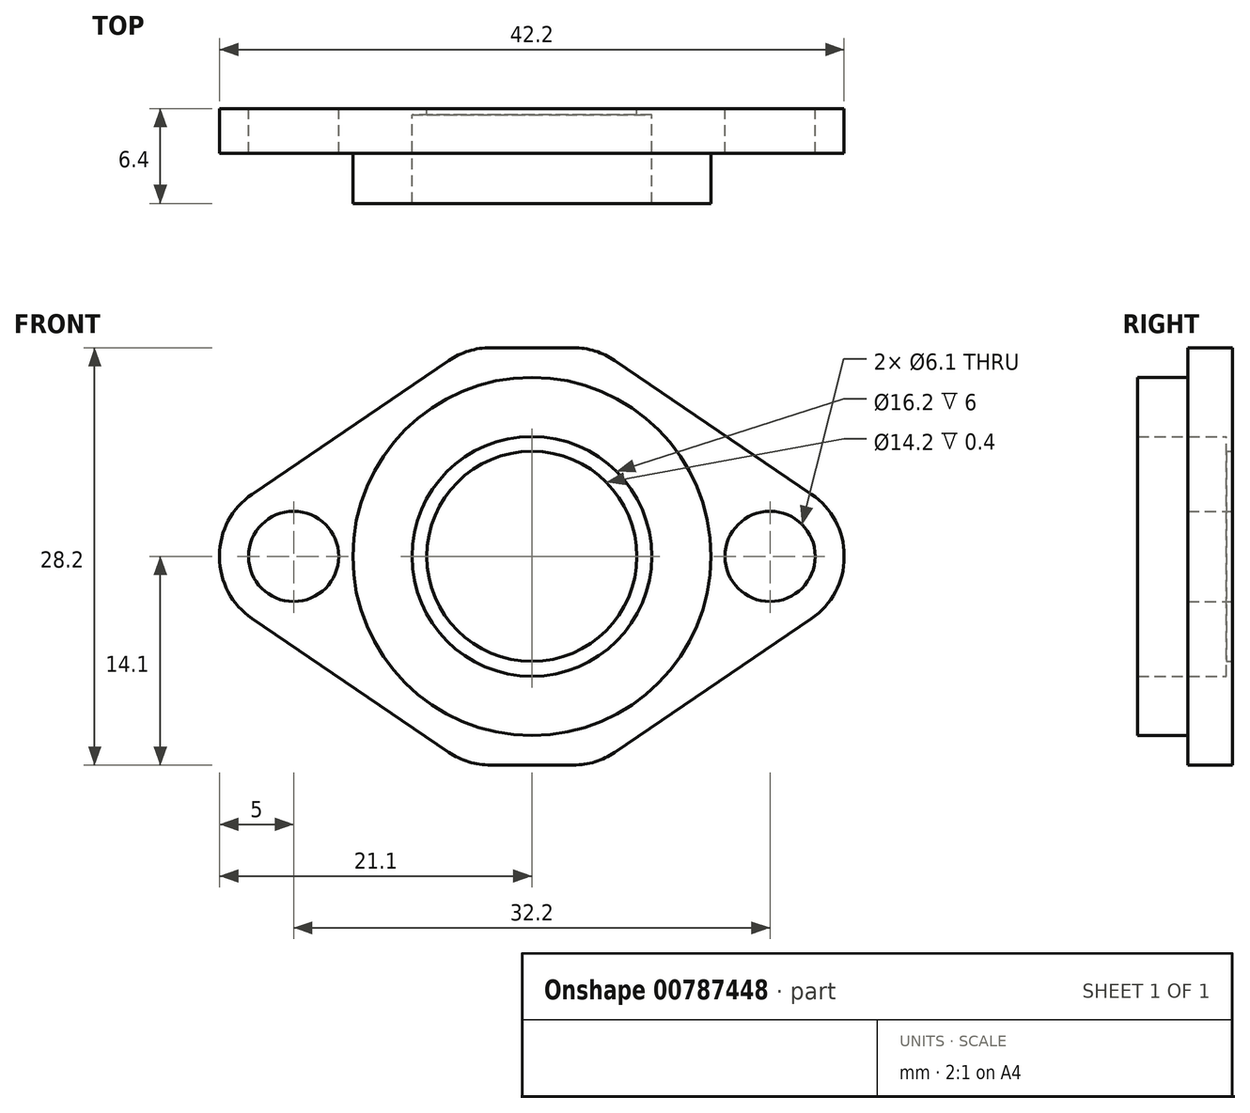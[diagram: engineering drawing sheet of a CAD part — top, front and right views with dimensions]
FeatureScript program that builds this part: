
annotation { "Feature Type Name" : "Feature", "Feature Type Description" : "" }
export const myFeature = defineFeature(function(context is Context, id is Id, definition is map)
    precondition{}
    {
        {
            var Q0;
            Q0=qCreatedBy(makeId("Front.planeOp"),FACE);
            var sketch = newSketch(context, id + "F0", { "sketchPlane" : qUnion([Q0])});
            skLineSegment(sketch, "E0.bottom", {"start": v(2.8, -14.1) * mm, "end": v(-2.8, -14.1) * mm});
            skLineSegment(sketch, "E0.top", {"start": v(2.8, 14.1) * mm, "end": v(-2.8, 14.1) * mm});
            skLineSegment(sketch, "E0.left", {"start": v(21.1, -0.06) * mm, "end": v(21.1, 0.06) * mm});
            skLineSegment(sketch, "E0.right", {"start": v(-21.1, -0.06) * mm, "end": v(-21.1, 0.06) * mm});
            skPoint(sketch, "E0.middle", {"position": v(0, 0) * mm});
            skCircle(sketch, "E1", {"center": v(-16.1, 0) * mm, "radius": 3.05 * mm});
            skCircle(sketch, "E2.MirrorC", {"center": v(16.1, 0) * mm, "radius": 3.05 * mm});
            skCircle(sketch, "E3", {"center": v(0, 0) * mm, "radius": 8.1 * mm});
            skCircle(sketch, "E4", {"center": v(0, 0) * mm, "radius": 12.1 * mm});
            skLineSegment(sketch, "E5", {"start": v(-17.81, 2.52) * mm, "end": v(-6.8, 10) * mm, "construction": true});
            skLineSegment(sketch, "E6", {"start": v(-18.91, 4.2) * mm, "end": v(-5.61, 13.24) * mm});
            skPoint(sketch, "E7.orphan", {"position": v(-21.1, 14.1) * mm});
            skPoint(sketch, "E8.visualSharp", {"position": v(-21.1, 2.7) * mm});
            skArc(sketch, "E8.filletArc", {"start": v(-18.91, 4.2) * mm, "mid": v(-20.52, 2.4) * mm, "end": v(-21.1, 0.06) * mm});
            skPoint(sketch, "E9.visualSharp", {"position": v(-4.34, 14.1) * mm});
            skArc(sketch, "E9.filletArc", {"start": v(-2.8, 14.1) * mm, "mid": v(-4.27, 13.88) * mm, "end": v(-5.61, 13.24) * mm});
            skArc(sketch, "E10.MirrorCS", {"start": v(2.8, 14.1) * mm, "mid": v(4.27, 13.88) * mm, "end": v(5.61, 13.24) * mm});
            skLineSegment(sketch, "E11.MirrorCS", {"start": v(18.91, 4.2) * mm, "end": v(5.61, 13.24) * mm});
            skArc(sketch, "E12.MirrorCS", {"start": v(18.91, 4.2) * mm, "mid": v(20.52, 2.4) * mm, "end": v(21.1, 0.06) * mm});
            skArc(sketch, "E13.MirrorCS", {"start": v(-18.91, -4.2) * mm, "mid": v(-20.52, -2.4) * mm, "end": v(-21.1, -0.06) * mm});
            skLineSegment(sketch, "E14.MirrorCS", {"start": v(-18.91, -4.2) * mm, "end": v(-5.61, -13.24) * mm});
            skArc(sketch, "E15.MirrorCS", {"start": v(-2.8, -14.1) * mm, "mid": v(-4.27, -13.88) * mm, "end": v(-5.61, -13.24) * mm});
            skArc(sketch, "E16.MirrorCS", {"start": v(2.8, -14.1) * mm, "mid": v(4.27, -13.88) * mm, "end": v(5.61, -13.24) * mm});
            skLineSegment(sketch, "E17.MirrorCS", {"start": v(18.91, -4.2) * mm, "end": v(5.61, -13.24) * mm});
            skArc(sketch, "E18.MirrorCS", {"start": v(18.91, -4.2) * mm, "mid": v(20.52, -2.4) * mm, "end": v(21.1, -0.06) * mm});
            skPoint(sketch, "E19.orphan", {"position": v(21.1, 14.1) * mm});
            skPoint(sketch, "E20.orphan", {"position": v(21.1, -14.1) * mm});
            skPoint(sketch, "E21.orphan", {"position": v(-21.1, -14.1) * mm});
            skSolve(sketch);
        }
        {
            var Q0;
            Q0=makeQuery(id+"F0.imprint","IMPRINT",FACE,{"disambiguationData":[TD([[makeQuery(id+"F0.imprint","IMPRINT",EDGE,{"derivedFrom":sQuery(id+"F0.wireOp",EDGE,"E3")}),-1.0]])]});
            extrude(context, id + "F1", {"entities" : qUnion([Q0]), "depth" : 6.4 * mm, "offsetDistance" : 25 * mm});
        }
        {
            var Q0;
            Q0=qSketchRegion(id+"F0",true);
            extrude(context, id + "F2", {"entities" : qUnion([Q0]), "operationType" : NewBodyOperationType.ADD, "depth" : 3 * mm, "offsetDistance" : 25 * mm});
        }
        {
            var Q0;
            {var subQ0=sQuery(id+"F0.wireOp",EDGE,"E4");Q0=makeQuery(id+"F2.boolean.opBoolean","MERGE",FACE,{"derivedFrom":[makeQuery(id+"F1.opExtrude","CAP_FACE",FACE,{"disambiguationData":[OSD([sQuery(id+"F0.wireOp",EDGE,"E3"),subQ0])],"isStart":true}),makeQuery(id+"F2.opExtrude","CAP_FACE",FACE,{"disambiguationData":[OSD([sQuery(id+"F0.wireOp",EDGE,"E0.bottom"),sQuery(id+"F0.wireOp",EDGE,"E0.top"),sQuery(id+"F0.wireOp",EDGE,"E0.left"),sQuery(id+"F0.wireOp",EDGE,"E0.right"),sQuery(id+"F0.wireOp",EDGE,"E1"),sQuery(id+"F0.wireOp",EDGE,"E2.MirrorC"),subQ0,sQuery(id+"F0.wireOp",EDGE,"E6"),sQuery(id+"F0.wireOp",EDGE,"E8.filletArc"),sQuery(id+"F0.wireOp",EDGE,"E9.filletArc"),sQuery(id+"F0.wireOp",EDGE,"E10.MirrorCS"),sQuery(id+"F0.wireOp",EDGE,"E11.MirrorCS"),sQuery(id+"F0.wireOp",EDGE,"E12.MirrorCS"),sQuery(id+"F0.wireOp",EDGE,"E13.MirrorCS"),sQuery(id+"F0.wireOp",EDGE,"E14.MirrorCS"),sQuery(id+"F0.wireOp",EDGE,"E15.MirrorCS"),sQuery(id+"F0.wireOp",EDGE,"E16.MirrorCS"),sQuery(id+"F0.wireOp",EDGE,"E17.MirrorCS"),sQuery(id+"F0.wireOp",EDGE,"E18.MirrorCS")])],"isStart":true})]});}
            var sketch = newSketch(context, id + "F3", { "sketchPlane" : qUnion([Q0])});
            skCircle(sketch, "E22", {"center": v(0, 0) * mm, "radius": 7.1 * mm});
            skSolve(sketch);
        }
        {
            var Q0;
            Q0=makeQuery(id+"F3.imprint","IMPRINT",FACE,{"disambiguationData":[TD([[makeQuery(id+"F3.imprint","IMPRINT",EDGE,{"derivedFrom":sQuery(id+"F3.wireOp",EDGE,"E22")}),-1.0]])]});
            extrude(context, id + "F4", {"entities" : qUnion([Q0]), "operationType" : NewBodyOperationType.ADD, "oppositeDirection" : true, "depth" : 0.4 * mm, "offsetDistance" : 25 * mm});
        }
    });
